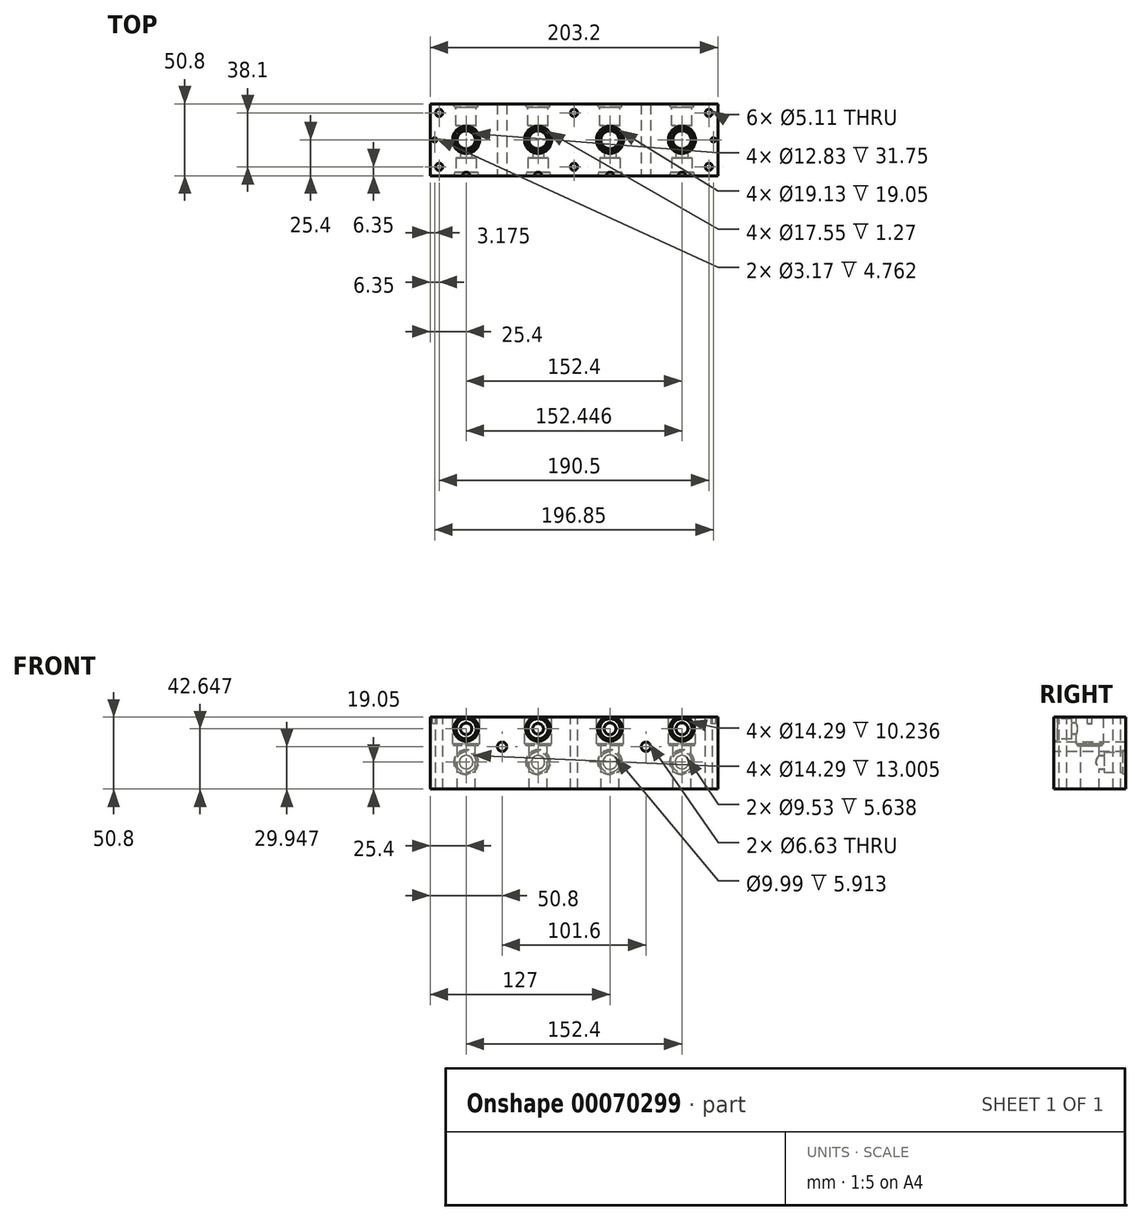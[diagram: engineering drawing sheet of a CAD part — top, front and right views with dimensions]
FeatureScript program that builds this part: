
annotation { "Feature Type Name" : "Feature", "Feature Type Description" : "" }
export const myFeature = defineFeature(function(context is Context, id is Id, definition is map)
    precondition{}
    {
        {
            var Q0;
            Q0=qCreatedBy(makeId("Top.planeOp"),FACE);
            var sketch = newSketch(context, id + "F0", { "sketchPlane" : qUnion([Q0])});
            skLineSegment(sketch, "E0.rect.bottom", {"start": v(101.6, 25.4) * mm, "end": v(-101.6, 25.4) * mm});
            skLineSegment(sketch, "E0.rect.top", {"start": v(101.6, -25.4) * mm, "end": v(-101.6, -25.4) * mm});
            skLineSegment(sketch, "E0.rect.left", {"start": v(101.6, 25.4) * mm, "end": v(101.6, -25.4) * mm});
            skLineSegment(sketch, "E0.rect.right", {"start": v(-101.6, 25.4) * mm, "end": v(-101.6, -25.4) * mm});
            skPoint(sketch, "E0.rect.middle", {"position": v(0, 0) * mm});
            skSolve(sketch);
        }
        {
            var Q0;
            Q0 = qSketchRegion(id + "F0", true);
            extrude(context, id + "F1", {"entities" : qUnion([Q0]), "depth" : 50.8 * mm});
        }
        {
            var Q0;
            Q0=makeQuery(id+"F1.opExtrude","CAP_FACE",FACE,{"disambiguationData":[OSD([sQuery(id+"F0.wireOp",EDGE,"E0.rect.bottom"),sQuery(id+"F0.wireOp",EDGE,"E0.rect.top"),sQuery(id+"F0.wireOp",EDGE,"E0.rect.left"),sQuery(id+"F0.wireOp",EDGE,"E0.rect.right")])],"isStart":false});
            var sketch = newSketch(context, id + "F2", { "sketchPlane" : qUnion([Q0])});
            skCircle(sketch, "E1", {"center": v(76.2, 0) * mm, "radius": 6.41 * mm});
            skCircle(sketch, "E2", {"center": v(25.4, 0) * mm, "radius": 6.41 * mm});
            skCircle(sketch, "E3", {"center": v(-25.4, 0) * mm, "radius": 6.41 * mm});
            skCircle(sketch, "E4", {"center": v(-76.2, 0) * mm, "radius": 6.41 * mm});
            skSolve(sketch);
        }
        {
            var Q0;
            Q0 = qSketchRegion(id + "F2", true);
            extrude(context, id + "F3", {"entities" : qUnion([Q0]), "operationType" : NewBodyOperationType.REMOVE, "endBound" : BoundingType.THROUGH_ALL, "oppositeDirection" : true, "depth" : 25.4 * mm});
        }
        {
            var Q0;
            Q0=makeQuery(id+"F1.opExtrude","CAP_FACE",FACE,{"disambiguationData":[OSD([sQuery(id+"F0.wireOp",EDGE,"E0.rect.bottom"),sQuery(id+"F0.wireOp",EDGE,"E0.rect.top"),sQuery(id+"F0.wireOp",EDGE,"E0.rect.left"),sQuery(id+"F0.wireOp",EDGE,"E0.rect.right")])],"isStart":false});
            var sketch = newSketch(context, id + "F4", { "sketchPlane" : qUnion([Q0])});
            skSolve(sketch);
        }
        {
            var Q0;
            Q0=makeQuery(id+"F4.imprint","IMPRINT",FACE,{"disambiguationData":[TD([[makeQuery(id+"F4.imprint","IMPRINT",EDGE,{"derivedFrom":makeQuery(id+"F1.opExtrude","CAP_EDGE",EDGE,{"disambiguationData":[OSD([sQuery(id+"F0.wireOp",EDGE,"E0.rect.bottom")])],"isStart":false})}),1.0]])]});
            var sketch = newSketch(context, id + "F5", { "sketchPlane" : qUnion([Q0])});
            skCircle(sketch, "E5", {"center": v(76.2, 0) * mm, "radius": 9.56 * mm});
            skCircle(sketch, "E6", {"center": v(25.4, 0) * mm, "radius": 9.56 * mm});
            skCircle(sketch, "E7", {"center": v(-25.4, 0) * mm, "radius": 9.56 * mm});
            skCircle(sketch, "E8", {"center": v(-76.2, 0) * mm, "radius": 9.56 * mm});
            skSolve(sketch);
        }
        {
            var Q0;
            Q0 = qSketchRegion(id + "F5", true);
            extrude(context, id + "F6", {"entities" : qUnion([Q0]), "operationType" : NewBodyOperationType.REMOVE, "oppositeDirection" : true, "depth" : 19.05 * mm});
        }
        {
            var Q0;
            Q0=makeQuery(id+"F1.opExtrude","SWEPT_FACE",FACE,{"disambiguationData":[OSD([sQuery(id+"F0.wireOp",EDGE,"E0.rect.top")])]});
            var sketch = newSketch(context, id + "F7", { "sketchPlane" : qUnion([Q0])});
            skCircle(sketch, "E9", {"center": v(76.2, 42.65) * mm, "radius": 4.25 * mm});
            skCircle(sketch, "E10", {"center": v(25.4, 42.65) * mm, "radius": 4.18 * mm});
            skCircle(sketch, "E11", {"center": v(-25.4, 42.65) * mm, "radius": 3.77 * mm});
            skCircle(sketch, "E12", {"center": v(-76.2, 42.65) * mm, "radius": 4.03 * mm});
            skSolve(sketch);
        }
        {
            var Q0;
            Q0 = qSketchRegion(id + "F7", true);
            extrude(context, id + "F8", {"entities" : qUnion([Q0]), "operationType" : NewBodyOperationType.REMOVE, "endBound" : BoundingType.UP_TO_NEXT, "oppositeDirection" : true, "depth" : 25.4 * mm});
        }
        {
            var Q0;
            Q0=makeQuery(id+"F1.opExtrude","SWEPT_FACE",FACE,{"disambiguationData":[OSD([sQuery(id+"F0.wireOp",EDGE,"E0.rect.top")])]});
            var sketch = newSketch(context, id + "F9", { "sketchPlane" : qUnion([Q0])});
            skCircle(sketch, "E13", {"center": v(76.2, 42.65) * mm, "radius": 7.14 * mm});
            skCircle(sketch, "E14", {"center": v(25.4, 42.65) * mm, "radius": 7.14 * mm});
            skCircle(sketch, "E15", {"center": v(-25.4, 42.65) * mm, "radius": 7.14 * mm});
            skCircle(sketch, "E16", {"center": v(-76.2, 42.65) * mm, "radius": 7.14 * mm});
            skSolve(sketch);
        }
        {
            var Q0;
            Q0 = qSketchRegion(id + "F9", true);
            extrude(context, id + "F10", {"entities" : qUnion([Q0]), "operationType" : NewBodyOperationType.REMOVE, "oppositeDirection" : true, "depth" : 12.7 * mm});
        }
        {
            var Q0;
            Q0=makeQuery(id+"F1.opExtrude","SWEPT_FACE",FACE,{"disambiguationData":[OSD([sQuery(id+"F0.wireOp",EDGE,"E0.rect.top")])]});
            var sketch = newSketch(context, id + "F11", { "sketchPlane" : qUnion([Q0])});
            skCircle(sketch, "E17", {"center": v(50.8, 29.95) * mm, "radius": 3.31 * mm});
            skPoint(sketch, "E17.centerSnap0", {"position": v(101.6, 29.95) * mm});
            skCircle(sketch, "E18", {"center": v(-50.8, 29.95) * mm, "radius": 3.31 * mm});
            skSolve(sketch);
        }
        {
            var Q0;
            Q0 = qSketchRegion(id + "F11", true);
            var Q1;
            Q1 = qSketchRegion(id + "F13", true);
            extrude(context, id + "F12", {"entities" : qUnion([Q0, Q1]), "operationType" : NewBodyOperationType.REMOVE, "endBound" : BoundingType.THROUGH_ALL, "oppositeDirection" : true, "depth" : 25.4 * mm});
        }
        {
            var Q0;
            Q0=makeQuery(id+"F4.imprint","IMPRINT",FACE,{"disambiguationData":[TD([[makeQuery(id+"F4.imprint","IMPRINT",EDGE,{"derivedFrom":makeQuery(id+"F1.opExtrude","CAP_EDGE",EDGE,{"disambiguationData":[OSD([sQuery(id+"F0.wireOp",EDGE,"E0.rect.bottom")])],"isStart":false})}),1.0]])]});
            var sketch = newSketch(context, id + "F13", { "sketchPlane" : qUnion([Q0])});
            skCircle(sketch, "E19", {"center": v(95.25, 19.05) * mm, "radius": 2.55 * mm});
            skCircle(sketch, "E20", {"center": v(95.25, -19.05) * mm, "radius": 2.55 * mm});
            skCircle(sketch, "E21", {"center": v(0, -19.05) * mm, "radius": 2.55 * mm});
            skCircle(sketch, "E22", {"center": v(0, 19.05) * mm, "radius": 2.55 * mm});
            skCircle(sketch, "E23", {"center": v(-95.25, 19.05) * mm, "radius": 2.55 * mm});
            skCircle(sketch, "E24", {"center": v(-95.25, -19.05) * mm, "radius": 2.55 * mm});
            skSolve(sketch);
        }
        {
            var Q0;
            Q0 = qSketchRegion(id + "F13", true);
            extrude(context, id + "F14", {"entities" : qUnion([Q0]), "operationType" : NewBodyOperationType.REMOVE, "oppositeDirection" : true, "depth" : 25.4 * mm});
        }
        {
            var Q0;
            Q0=makeQuery(id+"F1.opExtrude","CAP_FACE",FACE,{"disambiguationData":[OSD([sQuery(id+"F0.wireOp",EDGE,"E0.rect.bottom"),sQuery(id+"F0.wireOp",EDGE,"E0.rect.top"),sQuery(id+"F0.wireOp",EDGE,"E0.rect.left"),sQuery(id+"F0.wireOp",EDGE,"E0.rect.right")])],"isStart":true});
            var sketch = newSketch(context, id + "F15", { "sketchPlane" : qUnion([Q0])});
            skCircle(sketch, "E25", {"center": v(95.25, 19.05) * mm, "radius": 2.55 * mm});
            skCircle(sketch, "E26", {"center": v(95.25, -19.05) * mm, "radius": 2.55 * mm});
            skCircle(sketch, "E27", {"center": v(0, -19.05) * mm, "radius": 2.55 * mm});
            skCircle(sketch, "E28", {"center": v(0, 19.05) * mm, "radius": 2.55 * mm});
            skCircle(sketch, "E29", {"center": v(-95.25, 19.05) * mm, "radius": 2.55 * mm});
            skCircle(sketch, "E30", {"center": v(-95.25, -19.05) * mm, "radius": 2.55 * mm});
            skSolve(sketch);
        }
        {
            var Q0;
            Q0 = qSketchRegion(id + "F15", true);
            extrude(context, id + "F16", {"entities" : qUnion([Q0]), "operationType" : NewBodyOperationType.REMOVE, "oppositeDirection" : true, "depth" : 25.4 * mm});
        }
        {
            var Q0;
            Q0=makeQuery(id+"F1.opExtrude","SWEPT_FACE",FACE,{"disambiguationData":[OSD([sQuery(id+"F0.wireOp",EDGE,"E0.rect.bottom")])]});
            var sketch = newSketch(context, id + "F17", { "sketchPlane" : qUnion([Q0])});
            skCircle(sketch, "E31", {"center": v(-76.2, 19.05) * mm, "radius": 4.76 * mm});
            skCircle(sketch, "E32", {"center": v(-25.4, 19.05) * mm, "radius": 5 * mm});
            skCircle(sketch, "E33", {"center": v(25.4, 19.05) * mm, "radius": 4.65 * mm});
            skCircle(sketch, "E34", {"center": v(76.2, 19.05) * mm, "radius": 4.76 * mm});
            skSolve(sketch);
        }
        {
            var Q0;
            Q0 = qSketchRegion(id + "F17", true);
            extrude(context, id + "F18", {"entities" : qUnion([Q0]), "operationType" : NewBodyOperationType.REMOVE, "endBound" : BoundingType.UP_TO_NEXT, "oppositeDirection" : true, "depth" : 25.4 * mm});
        }
        {
            var Q0;
            Q0=makeQuery(id+"F6.boolean.opBoolean","COPY",FACE,{"derivedFrom":makeQuery(id+"F6.opExtrude","CAP_FACE",FACE,{"disambiguationData":[OSD([sQuery(id+"F5.wireOp",EDGE,"E8")])],"isStart":false})});
            var sketch = newSketch(context, id + "F19", { "sketchPlane" : qUnion([Q0])});
            skCircle(sketch, "E35", {"center": v(-76.2, 0) * mm, "radius": 7 * mm});
            skCircle(sketch, "E36", {"center": v(-76.2, 0) * mm, "radius": 8.78 * mm});
            skCircle(sketch, "E37", {"center": v(-25.18, 0) * mm, "radius": 7 * mm});
            skCircle(sketch, "E38", {"center": v(-25.18, 0) * mm, "radius": 8.78 * mm});
            skCircle(sketch, "E39", {"center": v(25.53, 0) * mm, "radius": 7 * mm});
            skCircle(sketch, "E40", {"center": v(25.53, 0) * mm, "radius": 8.78 * mm});
            skCircle(sketch, "E41", {"center": v(76.25, 0) * mm, "radius": 7 * mm});
            skCircle(sketch, "E42", {"center": v(76.25, 0) * mm, "radius": 8.78 * mm});
            skSolve(sketch);
        }
        {
            var Q0;
            Q0 = qSketchRegion(id + "F19", true);
            extrude(context, id + "F20", {"entities" : qUnion([Q0]), "operationType" : NewBodyOperationType.REMOVE, "oppositeDirection" : true, "depth" : 1.27 * mm});
        }
        {
            var Q0;
            Q0=makeQuery(id+"F4.imprint","IMPRINT",FACE,{"disambiguationData":[TD([[makeQuery(id+"F4.imprint","IMPRINT",EDGE,{"derivedFrom":makeQuery(id+"F1.opExtrude","CAP_EDGE",EDGE,{"disambiguationData":[OSD([sQuery(id+"F0.wireOp",EDGE,"E0.rect.bottom")])],"isStart":false})}),1.0]])]});
            var sketch = newSketch(context, id + "F21", { "sketchPlane" : qUnion([Q0])});
            skCircle(sketch, "E43", {"center": v(98.43, 0) * mm, "radius": 1.59 * mm});
            skCircle(sketch, "E44", {"center": v(-98.42, 0) * mm, "radius": 1.59 * mm});
            skSolve(sketch);
        }
        {
            var Q0;
            Q0 = qSketchRegion(id + "F21", true);
            extrude(context, id + "F22", {"entities" : qUnion([Q0]), "operationType" : NewBodyOperationType.REMOVE, "oppositeDirection" : true, "depth" : 4.76 * mm});
        }
        {
            var Q0;
            Q0=makeQuery(id+"F17.imprint","IMPRINT",FACE,{"disambiguationData":[TD([[makeQuery(id+"F17.imprint","IMPRINT",EDGE,{"derivedFrom":sQuery(id+"F17.wireOp",EDGE,"E31")}),-1.0]])]});
            var sketch = newSketch(context, id + "F23", { "sketchPlane" : qUnion([Q0])});
            skCircle(sketch, "E45", {"center": v(-76.2, 19.05) * mm, "radius": 8.74 * mm});
            skCircle(sketch, "E46", {"center": v(-25.4, 19.05) * mm, "radius": 8.74 * mm});
            skCircle(sketch, "E47", {"center": v(25.4, 19.05) * mm, "radius": 8.74 * mm});
            skCircle(sketch, "E48", {"center": v(76.2, 19.05) * mm, "radius": 8.74 * mm});
            skSolve(sketch);
        }
        {
            var Q0;
            Q0 = qSketchRegion(id + "F23", true);
            extrude(context, id + "F24", {"entities" : qUnion([Q0]), "operationType" : NewBodyOperationType.REMOVE, "oppositeDirection" : true, "depth" : 2.46 * mm, "hasDraft" : true, "draftAngle" : 12 * degree, "draftPullDirection" : true});
        }
        {
            var Q0;
            Q0=makeQuery(id+"F24.boolean.opBoolean","COPY",FACE,{"derivedFrom":makeQuery(id+"F24.opExtrude","CAP_FACE",FACE,{"disambiguationData":[OSD([sQuery(id+"F23.wireOp",EDGE,"E46")])],"isStart":false})});
            var sketch = newSketch(context, id + "F25", { "sketchPlane" : qUnion([Q0])});
            skCircle(sketch, "E49", {"center": v(-25.4, 19.05) * mm, "radius": 7.14 * mm});
            skCircle(sketch, "E50", {"center": v(-76.2, 19.05) * mm, "radius": 7.14 * mm});
            skCircle(sketch, "E51", {"center": v(25.4, 19.05) * mm, "radius": 7.14 * mm});
            skCircle(sketch, "E52", {"center": v(76.2, 19.05) * mm, "radius": 7.14 * mm});
            skSolve(sketch);
        }
        {
            var Q0;
            Q0 = qSketchRegion(id + "F25", true);
            extrude(context, id + "F26", {"entities" : qUnion([Q0]), "operationType" : NewBodyOperationType.REMOVE, "oppositeDirection" : true, "depth" : 13 * mm});
        }
        {
            var Q0;
            Q0=makeQuery(id+"F11.imprint","IMPRINT",FACE,{"disambiguationData":[TD([[makeQuery(id+"F11.imprint","IMPRINT",EDGE,{"derivedFrom":sQuery(id+"F11.wireOp",EDGE,"E17")}),-1.0]])]});
            var sketch = newSketch(context, id + "F27", { "sketchPlane" : qUnion([Q0])});
            skCircle(sketch, "E53", {"center": v(-76.2, 42.65) * mm, "radius": 8.74 * mm});
            skCircle(sketch, "E54", {"center": v(-25.4, 42.65) * mm, "radius": 8.74 * mm});
            skCircle(sketch, "E55", {"center": v(25.4, 42.65) * mm, "radius": 8.74 * mm});
            skCircle(sketch, "E56", {"center": v(76.2, 42.65) * mm, "radius": 8.74 * mm});
            skSolve(sketch);
        }
        {
            var Q0;
            Q0 = qSketchRegion(id + "F27", true);
            extrude(context, id + "F28", {"entities" : qUnion([Q0]), "operationType" : NewBodyOperationType.REMOVE, "oppositeDirection" : true, "depth" : 2.46 * mm, "hasDraft" : true, "draftAngle" : 12 * degree, "draftPullDirection" : true});
        }
    });
